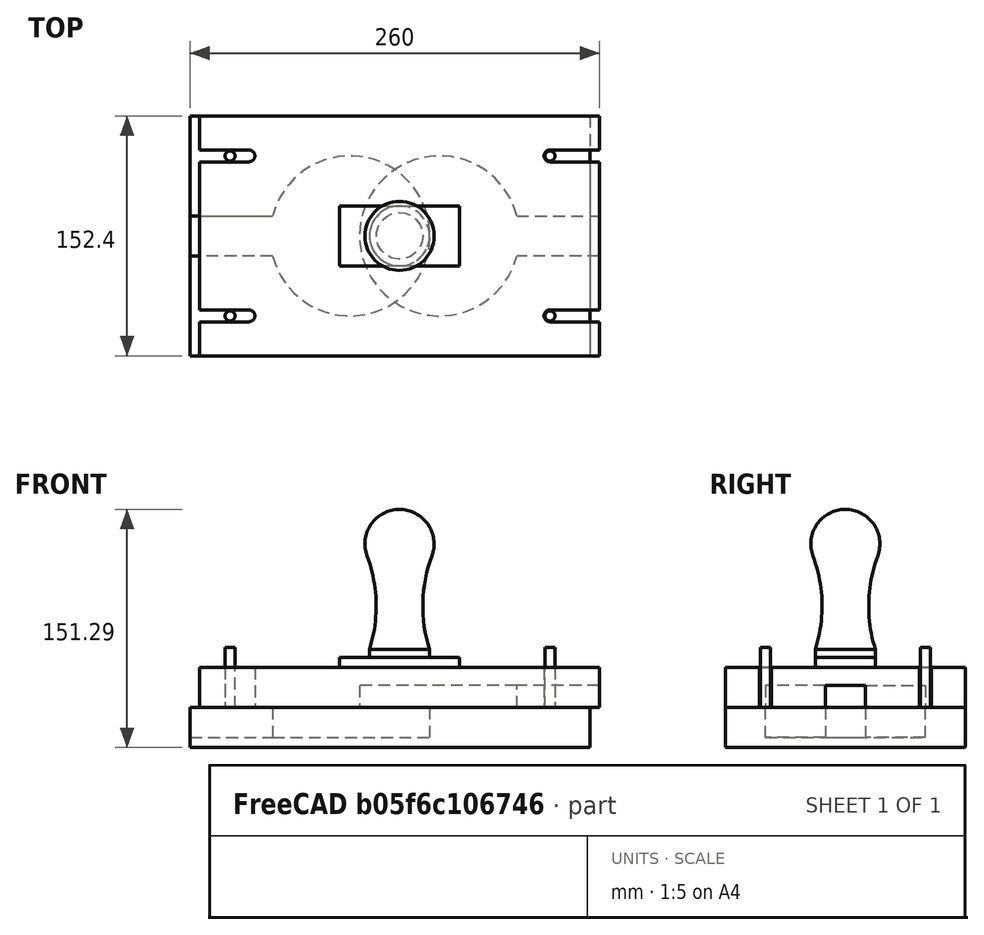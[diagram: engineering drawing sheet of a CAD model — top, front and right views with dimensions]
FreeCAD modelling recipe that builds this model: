
FCSTD DOCUMENT  (FreeCAD 0.17R13523 (Git))
Label: bell-metaldetector-FEM
License: All rights reserved
LicenseURL: http://en.wikipedia.org/wiki/All_rights_reserved
objects: Sketcher::SketchObject×8, PartDesign::Pad×4, PartDesign::Mirrored×4, PartDesign::Pocket×3, PartDesign::Body×3, PartDesign::MultiTransform×2, PartDesign::ShapeBinder×2, Fem::FemSolverObjectPython×2, Fem::FemMeshObjectPython×2, PartDesign::Revolution×1, Part::Fuse×1, Fem::ConstraintFixed×1, Fem::ConstraintForce×1, App::MaterialObjectPython×1, Fem::FemResultObjectPython×1, Fem::FemAnalysis×1
note: 36 computed .brp shape members not serialized (recipe doc carries the construction recipe); baked Part::Feature solids carry a one-line shape summary decoded from their .brp

FEATURE [Sketcher::SketchObject] Sketch
  MapMode = 5
  Support = -> [XY_Plane]
  sketch-geometry (4):
    g0: LineSegment StartX=-127 StartY=76.2 StartZ=0 EndX=127 EndY=76.2 EndZ=0
    g1: LineSegment StartX=127 StartY=76.2 StartZ=0 EndX=127 EndY=-76.2 EndZ=0
    g2: LineSegment StartX=127 StartY=-76.2 StartZ=0 EndX=-127 EndY=-76.2 EndZ=0
    g3: LineSegment StartX=-127 StartY=-76.2 StartZ=0 EndX=-127 EndY=76.2 EndZ=0
  constraints (11):
    c: Coincident(g0,g1)
    c: Coincident(g1,g2)
    c: Coincident(g2,g3)
    c: Coincident(g3,g0)
    c: Horizontal(g0)
    c: Horizontal(g2)
    c: Vertical(g1)
    c: Vertical(g3)
    c: DistanceX(g0,g0) = 254
    c: DistanceY(g1,g1) = 152.4
    c: Symmetric(g2,g0,g-1)
FEATURE [PartDesign::Pad] Pad
  Length = 25.4
  Length2 = 100
  Profile = -> Sketch
  Type = 0
FEATURE [Sketcher::SketchObject] Sketch001
  MapMode = 5
  Placement = pos=(0,0,25.4) rot=(0,0,1;0rad)
  Support = -> [Pad]
  sketch-geometry (1):
    g0: Circle CenterX=-101.6 CenterY=50.8 CenterZ=0 NormalX=0 NormalY=0 NormalZ=1 AngleXU=0 Radius=3.175
  constraints (3):
    c: DistanceX(g0) = -101.6
    c: Radius(g0) = 3.175
    c: DistanceY(g0) = 50.8
FEATURE [PartDesign::Pad] Pad001
  BaseFeature = -> Pad
  Length = 38.1
  Length2 = 100
  Profile = -> Sketch001
  Type = 0
FEATURE [PartDesign::Mirrored] Mirrored
  MirrorPlane = -> XZ_Plane
FEATURE [PartDesign::Mirrored] Mirrored001
  MirrorPlane = -> Sketch001 [V_Axis]
FEATURE [PartDesign::MultiTransform] MultiTransform
  BaseFeature = -> Pad001
  Originals = -> [Pad001]
  Transformations = -> [Mirrored,Mirrored001]
FEATURE [Sketcher::SketchObject] Sketch002
  ExternalGeometry = -> [MultiTransform]
  MapMode = 5
  Placement = pos=(0,0,25.4) rot=(0,0,1;0rad)
  Support = -> [MultiTransform]
  sketch-geometry (4):
    g0: ArcOfCircle CenterX=-25.4 CenterY=0 CenterZ=0 NormalX=0 NormalY=0 NormalZ=1 AngleXU=0 Radius=50.8 StartAngle=3.39427 EndAngle=9.1721
    g1: LineSegment StartX=-127 StartY=12.7 StartZ=0 EndX=-74.5869 EndY=12.7 EndZ=0
    g2: LineSegment StartX=-74.5869 StartY=-12.7 StartZ=0 EndX=-127 EndY=-12.7 EndZ=0
    g3: LineSegment StartX=-127 StartY=-12.7 StartZ=0 EndX=-127 EndY=12.7 EndZ=0
  constraints (13):
    c: PointOnObject(g0,g-1)
    c: Radius(g0) = 50.8
    c: Coincident(g2,g3)
    c: Coincident(g3,g1)
    c: Horizontal(g1)
    c: Horizontal(g2)
    c: Vertical(g3)
    c: Coincident(g0,g1)
    c: Symmetric(g1,g2,g-1)
    c: DistanceX(g0) = -25.4
    c: DistanceY(g3,g3) = 25.4
    c: Coincident(g2,g0)
    c: PointOnObject(g1,g-3)
FEATURE [PartDesign::Pocket] Pocket
  BaseFeature = -> MultiTransform
  Length = 19.05
  Length2 = 100
  Profile = -> Sketch002
  Type = 0
FEATURE [PartDesign::Body] Body  label="Bottom Block"
  Group = -> [Sketch,Pad,Sketch001,Pad001,MultiTransform,Mirrored,Mirrored001,Sketch002,Pocket]
  Origin = -> Origin
  Placement = pos=(-6,0,0) rot=(0,0,1;0rad)
  Tip = -> Pocket
FEATURE [PartDesign::ShapeBinder] ShapeBinder
  Support = -> [Pocket]
FEATURE [Sketcher::SketchObject] Sketch003
  ExternalGeometry = -> [ShapeBinder]
  MapMode = 5
  Placement = pos=(0,0,25.4) rot=(0,0,1;0rad)
  Support = -> [ShapeBinder]
  sketch-geometry (4):
    g0: LineSegment StartX=-127 StartY=76.2 StartZ=0 EndX=127 EndY=76.2 EndZ=0
    g1: LineSegment StartX=127 StartY=76.2 StartZ=0 EndX=127 EndY=-76.2 EndZ=0
    g2: LineSegment StartX=127 StartY=-76.2 StartZ=0 EndX=-127 EndY=-76.2 EndZ=0
    g3: LineSegment StartX=-127 StartY=-76.2 StartZ=0 EndX=-127 EndY=76.2 EndZ=0
  constraints (10):
    c: Coincident(g0,g1)
    c: Coincident(g1,g2)
    c: Coincident(g2,g3)
    c: Coincident(g3,g0)
    c: Horizontal(g0)
    c: Horizontal(g2)
    c: Vertical(g1)
    c: Vertical(g3)
    c: Coincident(g0,g-3)
    c: Coincident(g1,g-4)
FEATURE [PartDesign::Pad] Pad002
  Length = 25.5
  Length2 = 100
  Profile = -> Sketch003
  Type = 0
FEATURE [Sketcher::SketchObject] Sketch004
  ExternalGeometry = -> [ShapeBinder]
  MapMode = 5
  Placement = pos=(0,0,25.4) rot=(0,0,1;0rad)
  Support = -> [ShapeBinder]
  sketch-geometry (5):
    g0: LineSegment StartX=-127 StartY=54.55 StartZ=0 EndX=-95.6 EndY=54.55 EndZ=0
    g1: LineSegment StartX=-95.6 StartY=47.05 StartZ=0 EndX=-127 EndY=47.05 EndZ=0
    g2: LineSegment StartX=-127 StartY=47.05 StartZ=0 EndX=-127 EndY=54.55 EndZ=0
    g3: ArcOfCircle CenterX=-95.6 CenterY=50.8 CenterZ=0 NormalX=0 NormalY=0 NormalZ=1 AngleXU=0 Radius=3.75 StartAngle=4.71239 EndAngle=7.85398
    g4: LineSegment [constr] StartX=-101.6 StartY=50.8 StartZ=0 EndX=-95.6 EndY=50.8 EndZ=0
  constraints (13):
    c: Coincident(g1,g2)
    c: Coincident(g2,g0)
    c: Horizontal(g0)
    c: Horizontal(g1)
    c: Vertical(g2)
    c: PointOnObject(g0,g-4)
    c: Radius(g3) = 3.75
    c: Tangent(g3,g0) = 1.5708
    c: Tangent(g3,g1) = 1.5708
    c: Coincident(g4,g-3)
    c: Coincident(g4,g3)
    c: DistanceX(g4,g4) = 6
    c: Horizontal(g4)
FEATURE [PartDesign::Pocket] Pocket001
  BaseFeature = -> Pad002
  Length = 5
  Length2 = 100
  Profile = -> Sketch004
  Reversed = true
  Type = 1
FEATURE [PartDesign::Mirrored] Mirrored002
  MirrorPlane = -> YZ_Plane001
FEATURE [PartDesign::Mirrored] Mirrored003
  MirrorPlane = -> XZ_Plane001
FEATURE [PartDesign::MultiTransform] MultiTransform001
  BaseFeature = -> Pocket001
  Originals = -> [Pocket001]
  Transformations = -> [Mirrored002,Mirrored003]
FEATURE [Sketcher::SketchObject] Sketch005
  ExternalGeometry = -> [ShapeBinder]
  MapMode = 5
  Placement = pos=(0,0,25.4) rot=(0,0,1;0rad)
  Support = -> [ShapeBinder]
  sketch-geometry (5):
    g0: ArcOfCircle CenterX=25.4 CenterY=0 CenterZ=0 NormalX=0 NormalY=0 NormalZ=1 AngleXU=0 Radius=50.8 StartAngle=0.25268 EndAngle=6.03051
    g1: LineSegment StartX=74.5869 StartY=12.7 StartZ=0 EndX=127 EndY=12.7 EndZ=0
    g2: LineSegment StartX=127 StartY=12.7 StartZ=0 EndX=127 EndY=-12.7 EndZ=0
    g3: LineSegment StartX=127 StartY=-12.7 StartZ=0 EndX=74.5869 EndY=-12.7 EndZ=0
    g4: LineSegment [constr] StartX=-74.5869 StartY=12.7 StartZ=0 EndX=-74.5869 EndY=-12.7 EndZ=0
  constraints (16):
    c: PointOnObject(g0,g-1)
    c: Equal(g0,g-3)
    c: Symmetric(g0,g-3,g-2)
    c: Coincident(g1,g2)
    c: Coincident(g2,g3)
    c: Horizontal(g1)
    c: Horizontal(g3)
    c: Vertical(g2)
    c: PointOnObject(g2,g-4)
    c: Coincident(g0,g1)
    c: Coincident(g0,g3)
    c: Coincident(g3,g0)
    c: Symmetric(g1,g2,g-1)
    c: Coincident(g4,g-3)
    c: Coincident(g4,g-3)
    c: Equal(g2,g4)
FEATURE [PartDesign::Pocket] Pocket002
  BaseFeature = -> MultiTransform001
  Length = 14
  Length2 = 100
  Profile = -> Sketch005
  Reversed = true
  Type = 0
FEATURE [PartDesign::Body] Body001  label="Top Block"
  Group = -> [ShapeBinder,Sketch003,Pad002,Sketch004,Pocket001,MultiTransform001,Mirrored002,Mirrored003,Sketch005,Pocket002]
  Origin = -> Origin001
  Tip = -> Pocket002
FEATURE [PartDesign::ShapeBinder] ShapeBinder001
  Support = -> [Pocket002]
FEATURE [Sketcher::SketchObject] Sketch006
  MapMode = 5
  Placement = pos=(0,0,50.9) rot=(0,0,1;0rad)
  Support = -> [ShapeBinder001]
  sketch-geometry (4):
    g0: LineSegment StartX=-38.1 StartY=19.05 StartZ=0 EndX=38.1 EndY=19.05 EndZ=0
    g1: LineSegment StartX=38.1 StartY=19.05 StartZ=0 EndX=38.1 EndY=-19.05 EndZ=0
    g2: LineSegment StartX=38.1 StartY=-19.05 StartZ=0 EndX=-38.1 EndY=-19.05 EndZ=0
    g3: LineSegment StartX=-38.1 StartY=-19.05 StartZ=0 EndX=-38.1 EndY=19.05 EndZ=0
  constraints (11):
    c: Coincident(g0,g1)
    c: Coincident(g1,g2)
    c: Coincident(g2,g3)
    c: Coincident(g3,g0)
    c: Horizontal(g0)
    c: Horizontal(g2)
    c: Vertical(g1)
    c: Vertical(g3)
    c: Symmetric(g0,g2,g-1)
    c: DistanceX(g0,g0) = 76.2
    c: DistanceY(g1,g1) = 38.1
FEATURE [PartDesign::Pad] Pad003
  Length = 6.35
  Length2 = 100
  Profile = -> Sketch006
  Type = 0
FEATURE [Sketcher::SketchObject] Sketch007
  ExternalGeometry = -> [Pad003]
  MapMode = 5
  Placement = pos=(0,0,0) rot=(1,0,0;1.5708rad)
  Support = -> [XZ_Plane002]
  sketch-geometry (5):
    g0: ArcOfCircle CenterX=0 CenterY=129.37 CenterZ=0 NormalX=0 NormalY=0 NormalZ=1 AngleXU=0 Radius=21.92 StartAngle=5.92846 EndAngle=7.85398
    g1: ArcOfCircle CenterX=106.828 CenterY=89.8018 CenterZ=0 NormalX=0 NormalY=0 NormalZ=1 AngleXU=0 Radius=92 StartAngle=2.78687 EndAngle=3.44574
    g2: LineSegment StartX=19.05 StartY=62.25 StartZ=0 EndX=19.05 EndY=57.25 EndZ=0
    g3: LineSegment StartX=19.05 StartY=57.25 StartZ=0 EndX=1.1e-11 EndY=57.25 EndZ=0
    g4: LineSegment StartX=1.1e-11 StartY=57.25 StartZ=0 EndX=1.1e-11 EndY=151.29 EndZ=0
  constraints (16):
    c: PointOnObject(g0,g-2)
    c: Tangent(g1,g0) = 1.5708
    c: PointOnObject(g0,g-2)
    c: Coincident(g2,g1)
    c: PointOnObject(g2,g-3)
    c: Vertical(g2)
    c: Coincident(g2,g3)
    c: Coincident(g3,g4)
    c: Vertical(g4)
    c: Coincident(g0,g4)
    c: DistanceY(g2,g2) = 5
    c: Horizontal(g3)
    c: DistanceY(g4,g4) = 94.04
    c: DistanceX(g3,g3) = 19.05
    c: Radius(g1) = 92
    c: DistanceY(g3,g0) = 72.12
FEATURE [PartDesign::Revolution] Revolution
  Angle = 360
  Axis = (0,0,1)
  Base = (0,0,0)
  BaseFeature = -> Pad003
  Profile = -> Sketch007
  ReferenceAxis = -> Z_Axis002
  Reversed = true
FEATURE [PartDesign::Body] Body002  label="Handle"
  Group = -> [ShapeBinder001,Sketch006,Pad003,Sketch007,Revolution]
  Origin = -> Origin002
  Tip = -> Revolution
FEATURE [Part::Fuse] Fusion
  Base = -> Body001
  Tool = -> Body002
FEATURE [Fem::FemSolverObjectPython] CalculiXccxTools  # FEM object (typed FeaturePython)
  AnalysisType = 0
  BeamShellResultOutput3D = false
  EigenmodeHighLimit = 1000000
  EigenmodeLowLimit = 0
  EigenmodesCount = 10
  GeometricalNonlinearity = 0
  IterationsControlParameterCutb = 0.25,0.5,0.75,0.85,,,1.5,
  IterationsControlParameterIter = 4,8,9,200,10,400,,200,,
  IterationsControlParameterTimeUse = false
  IterationsThermoMechMaximum = 200
  IterationsUserDefinedIncrementations = false
  IterationsUserDefinedTimeStepLength = false
  MaterialNonlinearity = 0
  MatrixSolverType = 0
  SplitInputWriter = false
  ThermoMechSteadyState = true
  TimeEnd = 1
  TimeInitialStep = 1
FEATURE [Fem::FemMeshObjectPython] FEMMeshGmsh  # FEM object (typed FeaturePython)
  Algorithm2D = 0
  Algorithm3D = 0
  CharacteristicLengthMax = 0
  CharacteristicLengthMin = 0
  CoherenceMesh = true
  ElementDimension = 0
  ElementOrder = 1
  GeometryTolerance = 1e-06
  GroupsOfNodes = false
  HighOrderOptimize = false
  OptimizeNetgen = false
  OptimizeStd = true
  Part = -> Fusion
  RecombineAll = false
FEATURE [Fem::ConstraintFixed] FemConstraintFixed
  NormalDirection = (0,0,-1)
  Normals = (14) [(0,0,-1),(0,0,-1),(0,0,-1),(0,0,-1),(0,0,-1),(0,0,-1),(0,0,-1),(0,0,-1),(0,0,-1),(0,0,-1),(0,0,-1),(0,0,-1),(0,0,-1),(0,0,-1)]
  Points = (14) [(127,-76.2,25.4),(42.3333,-76.2,25.4),(-42.3333,-76.2,25.4),(-127,-76.2,25.4),(127,-25.4,25.4),(-42.3333,-25.4,25.4),(-127,-25.4,25.4),+7 more]
  References = -> [Fusion]
  Scale = 15
FEATURE [Fem::ConstraintForce] FemConstraintForce
  Direction = -> Fusion [Face20]
  DirectionVector = (1,0,0)
  Force = 9000
  NormalDirection = (-0.820772,2e-12,0.571256)
  Points = (44) [(20.5553,-6.84881e-11,121.756),(-10.2777,-17.8014,121.756),(-10.2777,17.8014,121.756),(20.5553,-6.84831e-11,121.756),(21.0227,-6.65809e-11,135.577),+39 more]
  References = -> [Fusion]
  Scale = 7
FEATURE [App::MaterialObjectPython] SolidMaterial  # material (typed FeaturePython)
  Category = 0
  Material = Density=700.0 kg/m^3,Description=A standard construction wood,Father=Aggregate,Name=Wood,PoissonRatio=0.05,+5 more (map truncated)
FEATURE [Fem::FemSolverObjectPython] CalculiXccxTools001  # FEM object (typed FeaturePython)
  AnalysisType = 0
  BeamShellResultOutput3D = false
  EigenmodeHighLimit = 1000000
  EigenmodeLowLimit = 0
  EigenmodesCount = 10
  GeometricalNonlinearity = 0
  IterationsControlParameterCutb = 0.25,0.5,0.75,0.85,,,1.5,
  IterationsControlParameterIter = 4,8,9,200,10,400,,200,,
  IterationsControlParameterTimeUse = false
  IterationsThermoMechMaximum = 200
  IterationsUserDefinedIncrementations = false
  IterationsUserDefinedTimeStepLength = false
  MaterialNonlinearity = 0
  MatrixSolverType = 0
  SplitInputWriter = false
  ThermoMechSteadyState = true
  TimeEnd = 1
  TimeInitialStep = 1
FEATURE [Fem::FemMeshObjectPython] Result_mesh  # FEM object (typed FeaturePython)
FEATURE [Fem::FemResultObjectPython] CalculiX_static_results  # FEM object (typed FeaturePython)
  DisplacementLengths = [0,8.1403e-05,0,4.09998e-05,0,5.47332e-05,0,7.1095e-05,0,0,0,0,0,0,0,0,0,0,0,0,0,0,0,0,0,0,0,0,0.000118487,0.000201965,0.000161582,0.000161575,0.000285996,0.000200135,0.000426076,0.000119691,0.000275486,5.56487e-05,0.000289169,8.18043e-05,+2838 more]
  DisplacementVectors = (2878) [(0,0,0),(6.64685e-05,-2.74203e-05,3.81642e-05),(0,0,0),(-5.82511e-06,-3.63502e-05,1.80476e-05),(0,0,0),(4.66126e-05,-2.74275e-05,8.40954e-06),(0,0,0),+2871 more]
  Eigenmode = 0
  EigenmodeFrequency = 0
  MaxShear = [0.0272864,0.00253766,0.0200174,0.0065484,0.00969071,0.00716712,0.0194921,0.0291469,0.0489875,0.0881967,0.049282,0.0490527,0.0801425,0.0508196,0.00975891,0.0274009,0.0176709,0.0196986,0.0704934,0.247394,0.0777387,0.0415483,2.76646,3.24839,+2854 more]
  Mesh = -> Result_mesh
  NodeNumbers = [1,2,3,4,5,6,7,8,9,10,11,12,13,14,15,16,17,18,19,20,21,22,23,24,25,26,27,28,29,30,31,32,33,34,35,36,37,38,39,40,41,42,43,44,45,46,47,48,49,50,51,52,53,54,55,56,57,58,59,60,61,62,63,64,65,66,67,68,69,+2809 more]
  PrincipalMax = [0.0497783,0.00071804,0.0312318,0.00366602,0.0156678,0.00382675,0.00254363,0.0161813,0.0550425,0.113944,0.0897616,0.0894468,0.107351,0.062652,0.0157387,0.050026,0.0263435,0.00290872,0.0810773,0.26311,0.00972118,0.0316626,1.92804,1.39034,+2854 more]
  PrincipalMed = [0.00151766,-0.00325236,0.00107366,-0.00394606,-0.000899496,-0.00610573,0.000479628,-0.0215486,0.00248314,0.00409552,0.00354916,0.00355231,0.00250758,0.00396689,-0.000898124,0.00152832,0.000762903,0.000621006,0.00233571,-0.0052862,+2858 more]
  PrincipalMin = [-0.00479456,-0.00435727,-0.00880292,-0.00943078,-0.00371362,-0.0105075,-0.0364406,-0.0421124,-0.0429324,-0.0624498,-0.00880237,-0.00865865,-0.0529343,-0.0389872,-0.00377914,-0.00477582,-0.00899834,-0.0364885,-0.0599095,-0.231678,-0.145756,+2857 more]
  ResultType = Fem::FemResultMechanical
  Stats = [-0.0399997,0.0429549,2.30027,-0.0318697,6.06373e-05,0.0313779,-0.706866,-0.0174147,0.49269,0,0.0589902,2.30214,0.00154737,4.966,127.527,-13.2978,2.48035,131.841,-50.0075,-0.296376,50.0924,-112.796,-3.00047,5.19278,0.000862354,2.74041,+13 more]
  StrainVectors = (2878) [(-8.97783e-08,-7.33413e-08,3.65072e-06),(-2.70297e-07,-4.56798e-08,-2.00893e-07),(6.68585e-09,-8.17065e-08,1.83771e-06),+2875 more]
  StressValues = [0.0517065,0.00462297,0.0361237,0.0113919,0.0181388,0.0127181,0.0379943,0.0512083,0.0849239,0.154288,0.0930054,0.0926057,0.140991,0.0883728,0.0182487,0.0519375,0.0316124,0.0383047,0.122376,0.429013,0.147172,0.0747489,4.914,5.9373,0.0742307,+2853 more]
  StressVectors = (2878) [(0.00118831,0.00137616,0.0439369),(-0.00341728,-0.000850226,-0.00262409),(0.00119558,0.000185382,0.0221216),(-0.00426966,0.000211717,-0.00565288),+2874 more]
  Time = 0
FEATURE [Fem::FemAnalysis] Analysis
  Group = -> [CalculiXccxTools,FEMMeshGmsh,FemConstraintFixed,FemConstraintForce,SolidMaterial,CalculiXccxTools001,CalculiX_static_results]
